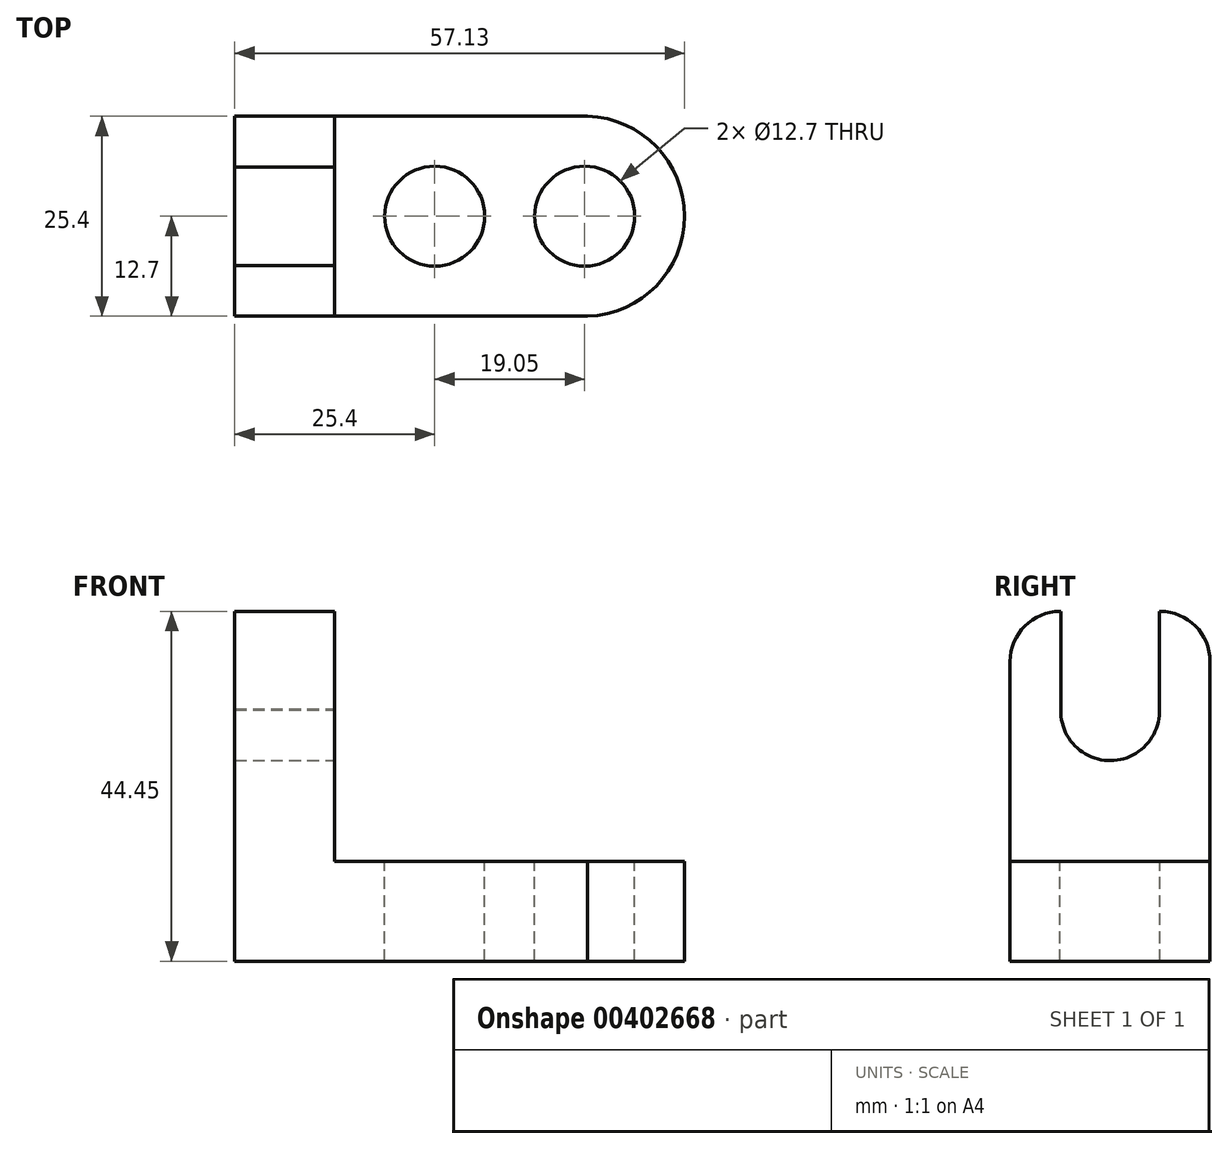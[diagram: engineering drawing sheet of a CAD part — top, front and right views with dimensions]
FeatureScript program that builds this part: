
annotation { "Feature Type Name" : "Feature", "Feature Type Description" : "" }
export const myFeature = defineFeature(function(context is Context, id is Id, definition is map)
    precondition{}
    {
        {
            var Q0;
            Q0=qCreatedBy(makeId("Front.planeOp"),FACE);
            var sketch = newSketch(context, id + "F0", { "sketchPlane" : qUnion([Q0])});
            skLineSegment(sketch, "E0", {"start": v(0, 0) * mm, "end": v(57.15, 0) * mm});
            skLineSegment(sketch, "E1", {"start": v(57.15, 12.7) * mm, "end": v(12.7, 12.7) * mm});
            skLineSegment(sketch, "E2", {"start": v(12.7, 12.7) * mm, "end": v(12.7, 44.45) * mm});
            skLineSegment(sketch, "E3", {"start": v(12.7, 44.45) * mm, "end": v(0, 44.45) * mm});
            skLineSegment(sketch, "E4", {"start": v(0, 44.45) * mm, "end": v(0, 0) * mm});
            skLineSegment(sketch, "E5", {"start": v(57.15, 12.7) * mm, "end": v(57.15, 0) * mm});
            skSolve(sketch);
        }
        {
            var Q0;
            Q0 = qSketchRegion(id + "F0", true);
            extrude(context, id + "F1", {"entities" : qUnion([Q0]), "depth" : 25.4 * mm});
        }
        {
            var Q0;
            Q0=makeQuery(id+"F1.opExtrude","SWEPT_FACE",FACE,{"disambiguationData":[OSD([sQuery(id+"F0.wireOp",EDGE,"E2")])]});
            var sketch = newSketch(context, id + "F2", { "sketchPlane" : qUnion([Q0])});
            skLineSegment(sketch, "E6", {"start": v(-25.4, 44.45) * mm, "end": v(-12.7, 44.45) * mm});
            skArc(sketch, "E7", {"start": v(-18.95, 31.93) * mm, "mid": v(-12.63, 25.5) * mm, "end": v(-6.45, 32.07) * mm});
            skLineSegment(sketch, "E8", {"start": v(-18.95, 31.57) * mm, "end": v(-18.95, 44.45) * mm});
            skLineSegment(sketch, "E9", {"start": v(-6.45, 32.07) * mm, "end": v(-6.45, 44.45) * mm});
            skSolve(sketch);
        }
        {
            var Q0;
            Q0 = qSketchRegion(id + "F2", true);
            var Q1;
            {var subQ6=sQuery(id+"F2.wireOp",EDGE,"E9");Q1=makeQuery(id+"F2.imprint","IMPRINT",FACE,{"disambiguationData":[TD([[makeQuery(id+"F2.imprint","IMPRINT",EDGE,{"derivedFrom":subQ6}),1.0]])]});}
            extrude(context, id + "F3", {"entities" : qUnion([Q0, Q1]), "operationType" : NewBodyOperationType.REMOVE, "oppositeDirection" : true, "depth" : 25.4 * mm});
        }
        {
            var Q0;
            Q0=makeQuery(id+"F1.opExtrude","CAP_EDGE",EDGE,{"disambiguationData":[OSD([sQuery(id+"F0.wireOp",EDGE,"E3")])],"isStart":false});
            fillet(context, id + "F4", {"entities" : qUnion([Q0]), "radius" : 6.35 * mm, "tangentPropagation" : true, "allowEdgeOverflow" : false});
        }
        {
            var Q0;
            Q0=makeQuery(id+"F1.opExtrude","CAP_EDGE",EDGE,{"disambiguationData":[OSD([sQuery(id+"F0.wireOp",EDGE,"E3")])],"isStart":true});
            fillet(context, id + "F5", {"entities" : qUnion([Q0]), "radius" : 6.35 * mm, "tangentPropagation" : true, "allowEdgeOverflow" : false});
        }
        {
            var Q0;
            Q0=makeQuery(id+"F1.opExtrude","SWEPT_FACE",FACE,{"disambiguationData":[OSD([sQuery(id+"F0.wireOp",EDGE,"E1")])]});
            var sketch = newSketch(context, id + "F6", { "sketchPlane" : qUnion([Q0])});
            skLineSegment(sketch, "E10", {"start": v(38.1, -12.7) * mm, "end": v(31.75, -12.7) * mm});
            skCircle(sketch, "E11", {"center": v(44.45, -12.7) * mm, "radius": 6.35 * mm});
            skCircle(sketch, "E12", {"center": v(25.4, -12.7) * mm, "radius": 6.35 * mm});
            skArc(sketch, "E13", {"start": v(44.45, -25.4) * mm, "mid": v(57.15, -12.7) * mm, "end": v(44.45, 0) * mm});
            skPoint(sketch, "E14.end.orphan", {"position": v(57.15, -12.7) * mm});
            skSolve(sketch);
        }
        {
            var Q0;
            Q0 = qSketchRegion(id + "F6", true);
            extrude(context, id + "F7", {"entities" : qUnion([Q0]), "operationType" : NewBodyOperationType.REMOVE, "oppositeDirection" : true, "depth" : 25.4 * mm});
        }
        {
            var Q0;
            Q0=makeQuery(id+"F1.opExtrude","SWEPT_FACE",FACE,{"disambiguationData":[OSD([sQuery(id+"F0.wireOp",EDGE,"E1")])]});
            var sketch = newSketch(context, id + "F8", { "sketchPlane" : qUnion([Q0])});
            skLineSegment(sketch, "E15", {"start": v(57.15, 0) * mm, "end": v(44.82, 0) * mm});
            skArc(sketch, "E16", {"start": v(44.82, -25.4) * mm, "mid": v(57.13, -12.7) * mm, "end": v(44.82, 0) * mm});
            skSolve(sketch);
        }
        {
            var Q0;
            Q0 = qSketchRegion(id + "F8", true);
            var Q1;
            Q1=makeQuery(id+"F8.imprint","IMPRINT",FACE,{"disambiguationData":[TD([[makeQuery(id+"F8.imprint","IMPRINT",EDGE,{"derivedFrom":sQuery(id+"F8.wireOp",EDGE,"E15")}),1.0]])]});
            extrude(context, id + "F9", {"entities" : qUnion([Q0, Q1]), "operationType" : NewBodyOperationType.REMOVE, "oppositeDirection" : true, "depth" : 25.4 * mm});
        }
    });
